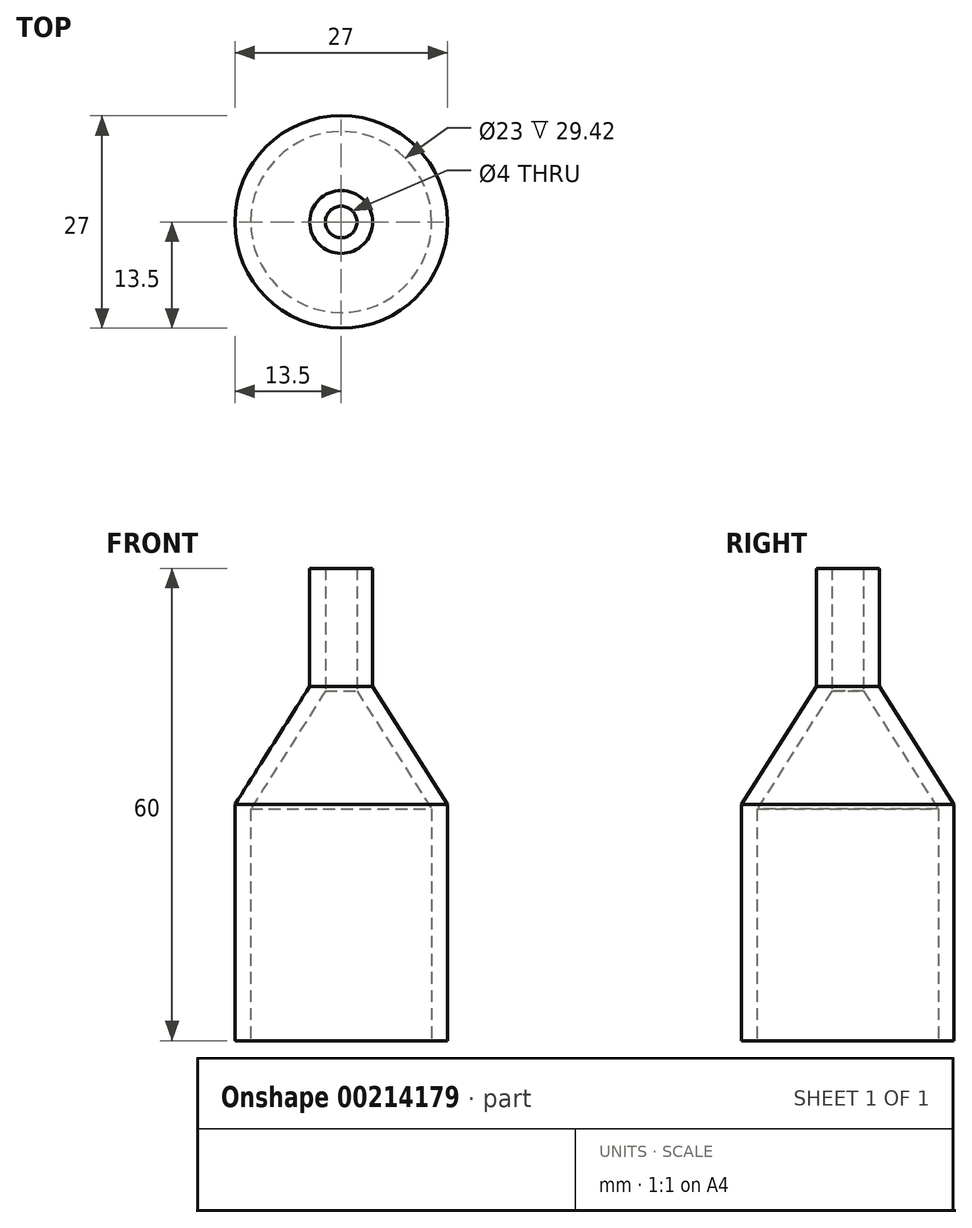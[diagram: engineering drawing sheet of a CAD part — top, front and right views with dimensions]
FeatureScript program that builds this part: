
annotation { "Feature Type Name" : "Feature", "Feature Type Description" : "" }
export const myFeature = defineFeature(function(context is Context, id is Id, definition is map)
    precondition{}
    {
        {
            var Q0;
            Q0=qCreatedBy(makeId("Front.planeOp"),FACE);
            var sketch = newSketch(context, id + "F0", { "sketchPlane" : qUnion([Q0])});
            skLineSegment(sketch, "E0", {"start": v(-13.5, 0) * mm, "end": v(-13.5, 30) * mm});
            skLineSegment(sketch, "E1", {"start": v(-13.5, 30) * mm, "end": v(-4, 45) * mm});
            skLineSegment(sketch, "E2", {"start": v(-4, 45) * mm, "end": v(-4, 60) * mm});
            skLineSegment(sketch, "E3", {"start": v(-11.5, 0) * mm, "end": v(-11.5, 29.42) * mm});
            skLineSegment(sketch, "E4", {"start": v(-11.5, 29.42) * mm, "end": v(-2, 44.42) * mm});
            skLineSegment(sketch, "E5", {"start": v(-2, 44.42) * mm, "end": v(-2, 60) * mm});
            skLineSegment(sketch, "E6", {"start": v(-11.5, 0) * mm, "end": v(-13.5, 0) * mm});
            skLineSegment(sketch, "E7", {"start": v(-2, 60) * mm, "end": v(-4, 60) * mm});
            skLineSegment(sketch, "E8", {"start": v(-11.5, 29.42) * mm, "end": v(-13.19, 30.5) * mm, "construction": true});
            skLineSegment(sketch, "E9", {"start": v(0, 0) * mm, "end": v(0, 60) * mm, "construction": true});
            skSolve(sketch);
        }
        {
            var Q0;
            Q0 = qSketchRegion(id + "F0", true);
            var Q1;
            Q1=sQuery(id+"F0.wireOp",EDGE,"E9");
            revolve(context, id + "F1", {"entities" : qUnion([Q0]), "axis" : qUnion([Q1]), "revolveType" : RevolveType.FULL});
        }
    });
